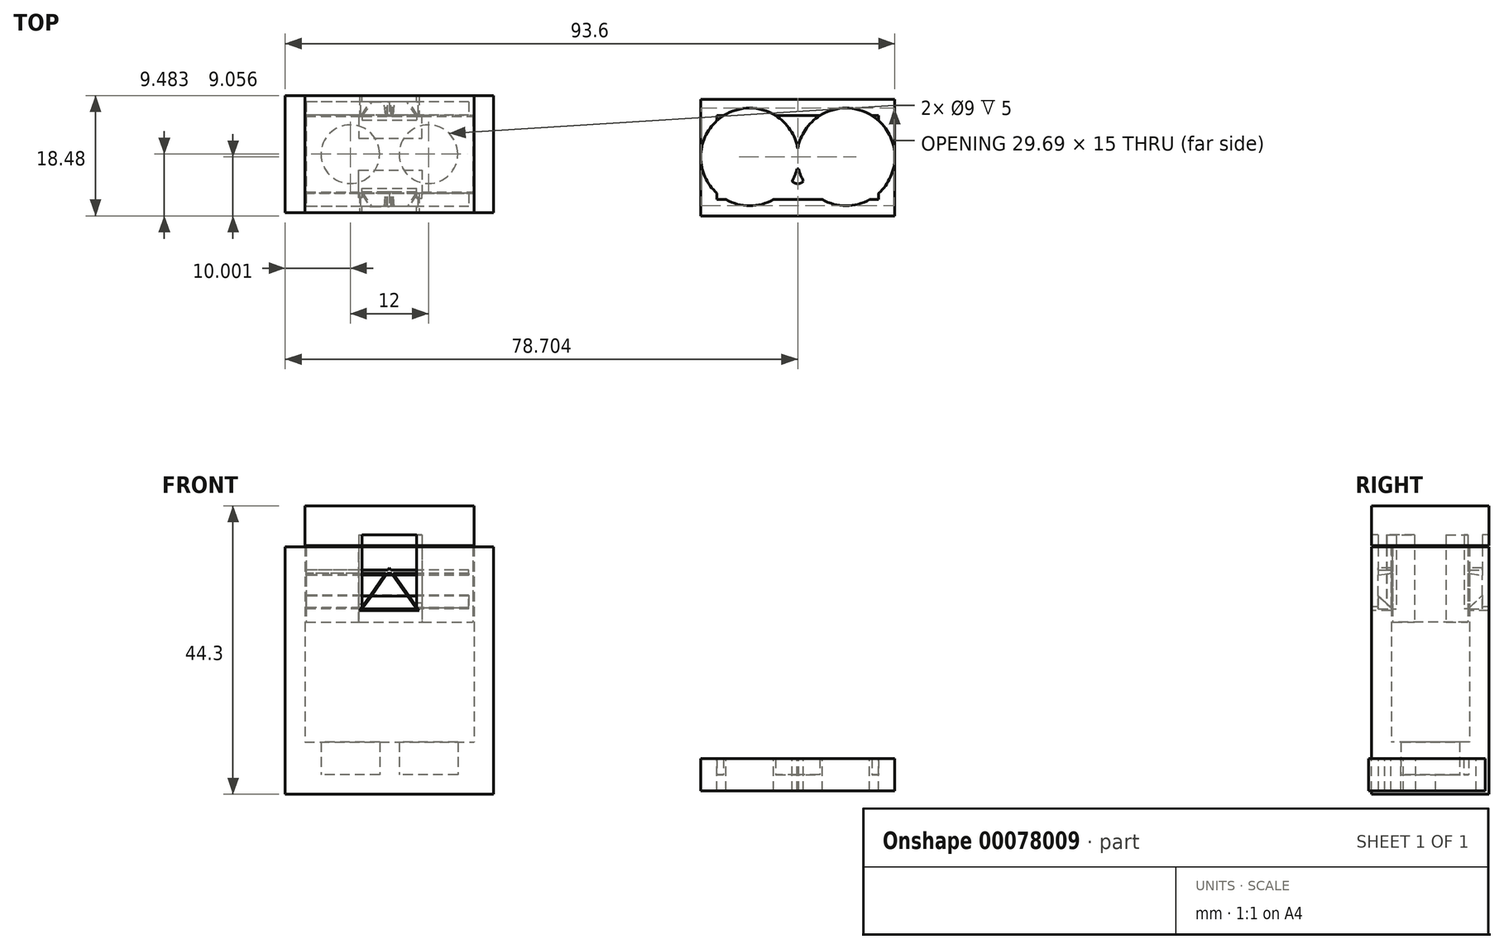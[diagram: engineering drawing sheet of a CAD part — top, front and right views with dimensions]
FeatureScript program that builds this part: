
annotation { "Feature Type Name" : "Feature", "Feature Type Description" : "" }
export const myFeature = defineFeature(function(context is Context, id is Id, definition is map)
    precondition{}
    {
        {
            var Q0;
            Q0=qCreatedBy(makeId("Top.planeOp"),FACE);
            var sketch = newSketch(context, id + "F0", { "sketchPlane" : qUnion([Q0])});
            skCircle(sketch, "E0", {"center": v(-25.55, 16.63) * mm, "radius": 4.5 * mm});
            skCircle(sketch, "E1.1.0.0", {"center": v(-13.55, 16.63) * mm, "radius": 4.5 * mm});
            skLineSegment(sketch, "E1.direction1", {"start": v(-25.55, 16.63) * mm, "end": v(-13.55, 16.63) * mm, "construction": true});
            skLineSegment(sketch, "E2.bottom", {"start": v(-32.55, 22.63) * mm, "end": v(-6.55, 22.63) * mm});
            skLineSegment(sketch, "E2.top", {"start": v(-32.55, 10.63) * mm, "end": v(-6.55, 10.63) * mm});
            skLineSegment(sketch, "E2.left", {"start": v(-32.55, 22.63) * mm, "end": v(-32.55, 10.63) * mm});
            skLineSegment(sketch, "E2.right", {"start": v(-6.55, 22.63) * mm, "end": v(-6.55, 10.63) * mm});
            skLineSegment(sketch, "E3", {"start": v(-25.55, 16.63) * mm, "end": v(-32.55, 16.63) * mm, "construction": true});
            skLineSegment(sketch, "E4", {"start": v(-19.55, 22.63) * mm, "end": v(-19.55, 16.63) * mm, "construction": true});
            skLineSegment(sketch, "E5", {"start": v(-19.55, 16.63) * mm, "end": v(-19.55, 10.63) * mm, "construction": true});
            skLineSegment(sketch, "E6.0", {"start": v(-35.55, 25.63) * mm, "end": v(-3.55, 25.63) * mm});
            skLineSegment(sketch, "E6.1", {"start": v(-35.55, 25.63) * mm, "end": v(-35.55, 7.63) * mm});
            skLineSegment(sketch, "E6.2", {"start": v(-35.55, 7.63) * mm, "end": v(-3.55, 7.63) * mm});
            skLineSegment(sketch, "E6.3", {"start": v(-3.55, 25.63) * mm, "end": v(-3.55, 7.63) * mm});
            skSolve(sketch);
        }
        {
            var Q0;
            Q0=makeQuery(id+"F0.imprint","IMPRINT",FACE,{"disambiguationData":[TD([[makeQuery(id+"F0.imprint","IMPRINT",EDGE,{"derivedFrom":sQuery(id+"F0.wireOp",EDGE,"E1.1.0.0")}),1.0]])]});
            var Q1;
            Q1=makeQuery(id+"F0.imprint","IMPRINT",FACE,{"disambiguationData":[TD([[makeQuery(id+"F0.imprint","IMPRINT",EDGE,{"derivedFrom":sQuery(id+"F0.wireOp",EDGE,"E0")}),-1.0]])]});
            var Q2;
            Q2=makeQuery(id+"F0.imprint","IMPRINT",FACE,{"disambiguationData":[TD([[makeQuery(id+"F0.imprint","IMPRINT",EDGE,{"derivedFrom":sQuery(id+"F0.wireOp",EDGE,"E2.bottom")}),1.0]])]});
            var Q3;
            Q3=makeQuery(id+"F0.imprint","IMPRINT",FACE,{"disambiguationData":[TD([[makeQuery(id+"F0.imprint","IMPRINT",EDGE,{"derivedFrom":sQuery(id+"F0.wireOp",EDGE,"E0")}),1.0]])]});
            extrude(context, id + "F1", {"entities" : qUnion([Q0, Q1, Q2, Q3]), "oppositeDirection" : true, "depth" : 3 * mm});
        }
        {
            var Q0;
            Q0=makeQuery(id+"F0.imprint","IMPRINT",FACE,{"disambiguationData":[TD([[makeQuery(id+"F0.imprint","IMPRINT",EDGE,{"derivedFrom":sQuery(id+"F0.wireOp",EDGE,"E0")}),-1.0]])]});
            extrude(context, id + "F2", {"entities" : qUnion([Q0]), "operationType" : NewBodyOperationType.ADD, "depth" : 5 * mm});
        }
        {
            var Q0;
            Q0=makeQuery(id+"F0.imprint","IMPRINT",FACE,{"disambiguationData":[TD([[makeQuery(id+"F0.imprint","IMPRINT",EDGE,{"derivedFrom":sQuery(id+"F0.wireOp",EDGE,"E2.bottom")}),1.0]])]});
            extrude(context, id + "F3", {"entities" : qUnion([Q0]), "operationType" : NewBodyOperationType.ADD, "depth" : 35 * mm});
        }
        {
            var Q0;
            {var subQ0=sQuery(id+"F0.wireOp",EDGE,"E6.2");Q0=makeQuery(id+"F3.boolean.opBoolean","MERGE",FACE,{"derivedFrom":[makeQuery(id+"F1.opExtrude","SWEPT_FACE",FACE,{"disambiguationData":[OSD([subQ0])]}),makeQuery(id+"F3.opExtrude","SWEPT_FACE",FACE,{"disambiguationData":[OSD([subQ0])]})]});}
            var sketch = newSketch(context, id + "F4", { "sketchPlane" : qUnion([Q0])});
            skLineSegment(sketch, "E7.0", {"start": v(-32.55, 0) * mm, "end": v(-6.55, 0) * mm});
            skLineSegment(sketch, "E8", {"start": v(-32.55, 0) * mm, "end": v(-32.55, 31.77) * mm});
            skLineSegment(sketch, "E9", {"start": v(-6.55, 0) * mm, "end": v(-6.55, 31.77) * mm});
            skLineSegment(sketch, "E10", {"start": v(-6.55, 31.77) * mm, "end": v(-32.55, 31.77) * mm});
            skLineSegment(sketch, "E11", {"start": v(-19.55, 31.77) * mm, "end": v(-19.55, 25.23) * mm, "construction": true});
            skLineSegment(sketch, "E12", {"start": v(-19.55, 25.23) * mm, "end": v(-14.96, 25.23) * mm});
            skLineSegment(sketch, "E13", {"start": v(-14.96, 25.23) * mm, "end": v(-19.55, 31.77) * mm});
            skLineSegment(sketch, "E14.MirrorCS", {"start": v(-19.55, 25.23) * mm, "end": v(-24.13, 25.23) * mm});
            skLineSegment(sketch, "E15.MirrorCS", {"start": v(-24.13, 25.23) * mm, "end": v(-19.55, 31.77) * mm});
            skLineSegment(sketch, "E16", {"start": v(-32.55, 25.46) * mm, "end": v(-6.55, 25.46) * mm});
            skLineSegment(sketch, "E17", {"start": v(-32.55, 31.77) * mm, "end": v(-32.55, 41.3) * mm});
            skLineSegment(sketch, "E18", {"start": v(-32.55, 41.3) * mm, "end": v(-6.55, 41.3) * mm});
            skLineSegment(sketch, "E19", {"start": v(-6.55, 41.3) * mm, "end": v(-6.55, 31.77) * mm});
            skSolve(sketch);
        }
        {
            var Q0;
            Q0=makeQuery(id+"F4.imprint","IMPRINT",FACE,{"disambiguationData":[TD([[makeQuery(id+"F4.imprint","IMPRINT",EDGE,{"derivedFrom":sQuery(id+"F4.wireOp",EDGE,"E12")}),1.0]])]});
            var Q1;
            {var subQ1=sQuery(id+"F4.wireOp",EDGE,"E13");var subQ3=sQuery(id+"F4.wireOp",EDGE,"E16");var subQ4=makeQuery(id+"F4.imprint","INTERSECT",VERTEX,{"derivedFrom":[subQ1,subQ3]});Q1=makeQuery(id+"F4.imprint","IMPRINT",FACE,{"disambiguationData":[TD([[makeQuery(id+"F4.imprint","IMPRINT",EDGE,{"disambiguationData":[TD([[subQ4,1.0]])],"derivedFrom":subQ3}),1.0]])]});}
            var Q2;
            {var subQ0=sQuery(id+"F0.wireOp",EDGE,"E6.0");Q2=makeQuery(id+"F3.boolean.opBoolean","MERGE",FACE,{"derivedFrom":[makeQuery(id+"F1.opExtrude","SWEPT_FACE",FACE,{"disambiguationData":[OSD([subQ0])]}),makeQuery(id+"F3.opExtrude","SWEPT_FACE",FACE,{"disambiguationData":[OSD([subQ0])]})]});}
            var Q3;
            Q3=makeQuery(id+"F1.opExtrude","SWEPT_BODY",BODY,{"disambiguationData":[OSD([sQuery(id+"F0.wireOp",EDGE,"E6.0"),sQuery(id+"F0.wireOp",EDGE,"E6.1"),sQuery(id+"F0.wireOp",EDGE,"E6.2"),sQuery(id+"F0.wireOp",EDGE,"E6.3")])]});
            extrude(context, id + "F5", {"entities" : qUnion([Q0, Q1]), "operationType" : NewBodyOperationType.REMOVE, "endBound" : BoundingType.UP_TO_SURFACE, "oppositeDirection" : true, "endBoundEntityFace" : qUnion([Q2]), "endBoundEntityBody" : qUnion([Q3]), "depth" : 25 * mm});
        }
        {
            var Q0;
            {var subQ0=sQuery(id+"F4.wireOp",EDGE,"E18");Q0=makeQuery(id+"F4.imprint","IMPRINT",FACE,{"disambiguationData":[TD([[makeQuery(id+"F4.imprint","IMPRINT",EDGE,{"derivedFrom":subQ0}),-1.0]])]});}
            var Q1;
            {var subQ0=sQuery(id+"F4.wireOp",EDGE,"E17");var subQ3=makeQuery(id+"F3.opExtrude","CAP_EDGE",EDGE,{"disambiguationData":[OSD([sQuery(id+"F0.wireOp",EDGE,"E6.2")])],"isStart":false});var subQ4=makeQuery(id+"F4.imprint","INTERSECT",VERTEX,{"derivedFrom":[subQ3,subQ0]});Q1=makeQuery(id+"F4.imprint","IMPRINT",FACE,{"disambiguationData":[TD([[makeQuery(id+"F4.imprint","IMPRINT",EDGE,{"disambiguationData":[TD([[subQ4,-1.0]])],"derivedFrom":subQ3}),-1.0]])]});}
            var Q2;
            {var subQ1=sQuery(id+"F4.wireOp",EDGE,"E8");var subQ3=sQuery(id+"F4.wireOp",EDGE,"E16");var subQ4=makeQuery(id+"F4.imprint","INTERSECT",VERTEX,{"derivedFrom":[subQ1,subQ3]});Q2=makeQuery(id+"F4.imprint","IMPRINT",FACE,{"disambiguationData":[TD([[makeQuery(id+"F4.imprint","IMPRINT",EDGE,{"disambiguationData":[TD([[subQ4,-1.0]])],"derivedFrom":subQ3}),1.0]])]});}
            var Q3;
            {var subQ1=sQuery(id+"F4.wireOp",EDGE,"E13");var subQ3=sQuery(id+"F4.wireOp",EDGE,"E16");var subQ4=makeQuery(id+"F4.imprint","INTERSECT",VERTEX,{"derivedFrom":[subQ1,subQ3]});Q3=makeQuery(id+"F4.imprint","IMPRINT",FACE,{"disambiguationData":[TD([[makeQuery(id+"F4.imprint","IMPRINT",EDGE,{"disambiguationData":[TD([[subQ4,1.0]])],"derivedFrom":subQ3}),1.0]])]});}
            var Q4;
            {var subQ1=sQuery(id+"F4.wireOp",EDGE,"E9");var subQ3=sQuery(id+"F4.wireOp",EDGE,"E16");var subQ4=makeQuery(id+"F4.imprint","INTERSECT",VERTEX,{"derivedFrom":[subQ1,subQ3]});Q4=makeQuery(id+"F4.imprint","IMPRINT",FACE,{"disambiguationData":[TD([[makeQuery(id+"F4.imprint","IMPRINT",EDGE,{"disambiguationData":[TD([[subQ4,1.0]])],"derivedFrom":subQ3}),1.0]])]});}
            var Q5;
            {var subQ0=sQuery(id+"F0.wireOp",EDGE,"E6.0");Q5=makeQuery(id+"F3.boolean.opBoolean","MERGE",FACE,{"derivedFrom":[makeQuery(id+"F1.opExtrude","SWEPT_FACE",FACE,{"disambiguationData":[OSD([subQ0])]}),makeQuery(id+"F3.opExtrude","SWEPT_FACE",FACE,{"disambiguationData":[OSD([subQ0])]})]});}
            extrude(context, id + "F6", {"entities" : qUnion([Q0, Q1, Q2, Q3, Q4]), "endBound" : BoundingType.UP_TO_SURFACE, "oppositeDirection" : true, "endBoundEntityFace" : qUnion([Q5]), "depth" : 25 * mm});
        }
        {
            var Q0;
            Q0=makeQuery(id+"F1.opExtrude","SWEPT_BODY",BODY,{"disambiguationData":[OSD([sQuery(id+"F0.wireOp",EDGE,"E6.0"),sQuery(id+"F0.wireOp",EDGE,"E6.1"),sQuery(id+"F0.wireOp",EDGE,"E6.2"),sQuery(id+"F0.wireOp",EDGE,"E6.3")])]});
            var Q1;
            Q1=makeQuery(id+"F6.opExtrude","SWEPT_BODY",BODY,{"disambiguationData":[OSD([sQuery(id+"F4.wireOp",EDGE,"E8"),sQuery(id+"F4.wireOp",EDGE,"E9"),sQuery(id+"F4.wireOp",EDGE,"E16"),sQuery(id+"F4.wireOp",EDGE,"E17"),sQuery(id+"F4.wireOp",EDGE,"E18"),sQuery(id+"F4.wireOp",EDGE,"E19")])]});
            booleanBodies(context, id + "F7", {"operationType" : BooleanOperationType.SUBTRACTION, "tools" : qUnion([Q0]), "targets" : qUnion([Q1]), "offset" : true, "offsetAll" : true, "offsetDistance" : 0.2 * mm, "keepTools" : true});
        }
        {
            var Q0;
            Q0=makeQuery(id+"F6.opExtrude","SWEPT_FACE",FACE,{"disambiguationData":[OSD([sQuery(id+"F4.wireOp",EDGE,"E16")])]});
            var sketch = newSketch(context, id + "F8", { "sketchPlane" : qUnion([Q0])});
            skLineSegment(sketch, "E20", {"start": v(-23.73, -10.83) * mm, "end": v(-23.73, -11.42) * mm});
            skLineSegment(sketch, "E21", {"start": v(-23.73, -11.42) * mm, "end": v(-15.37, -11.42) * mm});
            skLineSegment(sketch, "E22", {"start": v(-15.37, -10.83) * mm, "end": v(-15.37, -11.42) * mm});
            skLineSegment(sketch, "E23", {"start": v(-24.25, -10.83) * mm, "end": v(-24.25, -14.2) * mm});
            skLineSegment(sketch, "E24", {"start": v(-24.25, -14.2) * mm, "end": v(-14.57, -14.2) * mm});
            skLineSegment(sketch, "E25", {"start": v(-14.57, -14.2) * mm, "end": v(-14.57, -10.83) * mm});
            skLineSegment(sketch, "E26", {"start": v(-23.73, -8.63) * mm, "end": v(-15.37, -8.63) * mm});
            skLineSegment(sketch, "E27", {"start": v(-32.35, -16.63) * mm, "end": v(-6.75, -16.63) * mm, "construction": true});
            skLineSegment(sketch, "E28.MirrorCS", {"start": v(-24.25, -19.07) * mm, "end": v(-14.57, -19.07) * mm});
            skLineSegment(sketch, "E29.MirrorCS", {"start": v(-14.57, -19.07) * mm, "end": v(-14.57, -22.43) * mm});
            skLineSegment(sketch, "E30.MirrorCS", {"start": v(-23.73, -21.85) * mm, "end": v(-15.37, -21.85) * mm});
            skLineSegment(sketch, "E31.MirrorCS", {"start": v(-24.25, -22.43) * mm, "end": v(-24.25, -19.07) * mm});
            skLineSegment(sketch, "E32.MirrorCS", {"start": v(-23.73, -22.43) * mm, "end": v(-23.73, -21.85) * mm});
            skLineSegment(sketch, "E33.MirrorCS", {"start": v(-15.37, -22.43) * mm, "end": v(-15.37, -21.85) * mm});
            skLineSegment(sketch, "E34.MirrorCS", {"start": v(-23.73, -24.64) * mm, "end": v(-15.37, -24.64) * mm});
            skLineSegment(sketch, "E35", {"start": v(-24.25, -10.83) * mm, "end": v(-24.25, -9.96) * mm});
            skLineSegment(sketch, "E36", {"start": v(-24.25, -9.96) * mm, "end": v(-23.73, -9.96) * mm});
            skLineSegment(sketch, "E37", {"start": v(-14.57, -10.83) * mm, "end": v(-14.57, -9.88) * mm});
            skLineSegment(sketch, "E38", {"start": v(-14.57, -9.88) * mm, "end": v(-15.37, -9.88) * mm});
            skSolve(sketch);
        }
        {
            var Q0;
            {var subQ2=sQuery(id+"F8.wireOp",EDGE,"E20");Q0=makeQuery(id+"F8.imprint","IMPRINT",FACE,{"disambiguationData":[TD([[makeQuery(id+"F8.imprint","IMPRINT",EDGE,{"derivedFrom":subQ2}),-1.0]])]});}
            var Q1;
            {var subQ0=sQuery(id+"F8.wireOp",EDGE,"E26");Q1=makeQuery(id+"F8.imprint","IMPRINT",FACE,{"disambiguationData":[TD([[makeQuery(id+"F8.imprint","IMPRINT",EDGE,{"derivedFrom":subQ0}),1.0]])]});}
            var Q2;
            {var subQ0=sQuery(id+"F8.wireOp",EDGE,"E34.MirrorCS");Q2=makeQuery(id+"F8.imprint","IMPRINT",FACE,{"disambiguationData":[TD([[makeQuery(id+"F8.imprint","IMPRINT",EDGE,{"derivedFrom":subQ0}),-1.0]])]});}
            var Q3;
            {var subQ0=sQuery(id+"F8.wireOp",EDGE,"E37");Q3=makeQuery(id+"F8.imprint","IMPRINT",FACE,{"disambiguationData":[TD([[makeQuery(id+"F8.imprint","IMPRINT",EDGE,{"derivedFrom":subQ0}),1.0]])]});}
            var Q4;
            {var subQ0=sQuery(id+"F8.wireOp",EDGE,"E35");Q4=makeQuery(id+"F8.imprint","IMPRINT",FACE,{"disambiguationData":[TD([[makeQuery(id+"F8.imprint","IMPRINT",EDGE,{"derivedFrom":subQ0}),-1.0]])]});}
            var Q5;
            Q5=makeQuery(id+"F8.imprint","IMPRINT",FACE,{"disambiguationData":[TD([[makeQuery(id+"F8.imprint","IMPRINT",EDGE,{"derivedFrom":sQuery(id+"F8.wireOp",EDGE,"E28.MirrorCS")}),-1.0]])]});
            extrude(context, id + "F9", {"entities" : qUnion([Q0, Q1, Q2, Q3, Q4, Q5]), "operationType" : NewBodyOperationType.REMOVE, "oppositeDirection" : true, "depth" : 11.34 * mm});
        }
        {
            var Q0;
            Q0=makeQuery(id+"F9.boolean.opBoolean","SPLIT",FACE,{"disambiguationData":[TD([makeQuery(id+"F7.tempBoolean.opBoolean","COPY",FACE,{"derivedFrom":makeQuery(id+"F7.offsetTempBody.opPattern","COPY",FACE,{"derivedFrom":makeQuery(id+"F3.opExtrude","SWEPT_FACE",FACE,{"disambiguationData":[OSD([sQuery(id+"F0.wireOp",EDGE,"E2.left")])]}),"instanceName":"1"})})])],"derivedFrom":makeQuery(id+"F6.opExtrude","SWEPT_FACE",FACE,{"disambiguationData":[OSD([sQuery(id+"F4.wireOp",EDGE,"E16")])]})});
            extrude(context, id + "F10", {"entities" : qUnion([Q0]), "operationType" : NewBodyOperationType.ADD, "depth" : 2 * mm});
        }
        {
            var Q0;
            {var subQ0=sQuery(id+"F0.wireOp",EDGE,"E2.left");Q0=makeQuery(id+"F10.boolean.opBoolean","MERGE",FACE,{"derivedFrom":[makeQuery(id+"F7.tempBoolean.opBoolean","COPY",FACE,{"derivedFrom":makeQuery(id+"F7.offsetTempBody.opPattern","COPY",FACE,{"derivedFrom":makeQuery(id+"F3.opExtrude","SWEPT_FACE",FACE,{"disambiguationData":[OSD([subQ0])]}),"instanceName":"1"})}),makeQuery(id+"F10.opExtrude","SWEPT_FACE",FACE,{"disambiguationData":[OSD([subQ0,sQuery(id+"F4.wireOp",EDGE,"E16")])]})]});}
            var sketch = newSketch(context, id + "F11", { "sketchPlane" : qUnion([Q0])});
            skLineSegment(sketch, "E39.0", {"start": v(-24.64, 31.43) * mm, "end": v(-22.43, 31.43) * mm});
            skLineSegment(sketch, "E40.0", {"start": v(-24.64, 25.46) * mm, "end": v(-24.64, 31.43) * mm});
            skLineSegment(sketch, "E41.0", {"start": v(-24.64, 25.46) * mm, "end": v(-22.43, 25.46) * mm});
            skLineSegment(sketch, "E42.0", {"start": v(-10.83, 25.46) * mm, "end": v(-8.63, 25.46) * mm});
            skLineSegment(sketch, "E43.0", {"start": v(-8.63, 25.46) * mm, "end": v(-8.63, 31.43) * mm});
            skLineSegment(sketch, "E44.0", {"start": v(-10.83, 31.43) * mm, "end": v(-8.63, 31.43) * mm});
            skLineSegment(sketch, "E45", {"start": v(-24.64, 27.58) * mm, "end": v(-22.43, 25.46) * mm});
            skLineSegment(sketch, "E46", {"start": v(-8.63, 27.46) * mm, "end": v(-10.83, 25.46) * mm});
            skLineSegment(sketch, "E47", {"start": v(-24.64, 30.63) * mm, "end": v(-22.43, 30.92) * mm});
            skLineSegment(sketch, "E48", {"start": v(-10.83, 30.92) * mm, "end": v(-8.63, 30.7) * mm});
            skSolve(sketch);
        }
        {
            var Q0;
            {var subQ0=sQuery(id+"F11.wireOp",EDGE,"E39.0");Q0=makeQuery(id+"F11.imprint","IMPRINT",FACE,{"disambiguationData":[TD([[makeQuery(id+"F11.imprint","IMPRINT",EDGE,{"derivedFrom":subQ0}),-1.0]])]});}
            var Q1;
            {var subQ0=sQuery(id+"F11.wireOp",EDGE,"E41.0");Q1=makeQuery(id+"F11.imprint","IMPRINT",FACE,{"disambiguationData":[TD([[makeQuery(id+"F11.imprint","IMPRINT",EDGE,{"derivedFrom":subQ0}),1.0]])]});}
            var Q2;
            {var subQ0=sQuery(id+"F11.wireOp",EDGE,"E42.0");Q2=makeQuery(id+"F11.imprint","IMPRINT",FACE,{"disambiguationData":[TD([[makeQuery(id+"F11.imprint","IMPRINT",EDGE,{"derivedFrom":subQ0}),1.0]])]});}
            var Q3;
            {var subQ0=sQuery(id+"F11.wireOp",EDGE,"E44.0");Q3=makeQuery(id+"F11.imprint","IMPRINT",FACE,{"disambiguationData":[TD([[makeQuery(id+"F11.imprint","IMPRINT",EDGE,{"derivedFrom":subQ0}),-1.0]])]});}
            extrude(context, id + "F12", {"entities" : qUnion([Q0, Q1, Q2, Q3]), "operationType" : NewBodyOperationType.REMOVE, "oppositeDirection" : true, "depth" : 25 * mm});
        }
        {
            var Q0;
            Q0=qCreatedBy(makeId("Top.planeOp"),FACE);
            var sketch = newSketch(context, id + "F13", { "sketchPlane" : qUnion([Q0])});
            skLineSegment(sketch, "E49.bottom", {"start": v(30.75, 22.55) * mm, "end": v(55.55, 22.55) * mm});
            skLineSegment(sketch, "E49.top", {"start": v(30.75, 9.65) * mm, "end": v(55.55, 9.65) * mm});
            skLineSegment(sketch, "E49.left", {"start": v(30.75, 22.55) * mm, "end": v(30.75, 9.65) * mm});
            skLineSegment(sketch, "E49.right", {"start": v(55.55, 22.55) * mm, "end": v(55.55, 9.65) * mm});
            skLineSegment(sketch, "E50", {"start": v(43.15, 22.55) * mm, "end": v(43.15, 9.65) * mm, "construction": true});
            skCircle(sketch, "E51", {"center": v(43.15, 13.25) * mm, "radius": 1.15 * mm});
            skLineSegment(sketch, "E52.0", {"start": v(28.25, 25.05) * mm, "end": v(58.05, 25.05) * mm});
            skLineSegment(sketch, "E52.1", {"start": v(28.25, 25.05) * mm, "end": v(28.25, 7.15) * mm});
            skLineSegment(sketch, "E52.2", {"start": v(28.25, 7.15) * mm, "end": v(58.05, 7.15) * mm});
            skLineSegment(sketch, "E52.3", {"start": v(58.05, 25.05) * mm, "end": v(58.05, 7.15) * mm});
            skLineSegment(sketch, "E53", {"start": v(30.75, 16.1) * mm, "end": v(55.55, 16.1) * mm, "construction": true});
            skCircle(sketch, "E54", {"center": v(35.76, 16.2) * mm, "radius": 7.5 * mm});
            skCircle(sketch, "E55.MirrorC", {"center": v(50.55, 16.2) * mm, "radius": 7.5 * mm});
            skSolve(sketch);
        }
        {
            var Q0;
            Q0=makeQuery(id+"F13.imprint","IMPRINT",FACE,{"disambiguationData":[TD([[makeQuery(id+"F13.imprint","IMPRINT",EDGE,{"derivedFrom":sQuery(id+"F13.wireOp",EDGE,"E49.bottom")}),1.0]])]});
            var Q1;
            Q1=makeQuery(id+"F13.imprint","IMPRINT",FACE,{"disambiguationData":[TD([[makeQuery(id+"F13.imprint","IMPRINT",EDGE,{"derivedFrom":sQuery(id+"F13.wireOp",EDGE,"E49.bottom")}),-1.0]])]});
            var Q2;
            Q2=makeQuery(id+"F13.imprint","IMPRINT",FACE,{"disambiguationData":[TD([[makeQuery(id+"F13.imprint","IMPRINT",EDGE,{"derivedFrom":sQuery(id+"F13.wireOp",EDGE,"E51")}),1.0]])]});
            extrude(context, id + "F14", {"entities" : qUnion([Q0, Q1, Q2]), "oppositeDirection" : true, "depth" : 2.5 * mm});
        }
        {
            var Q0;
            Q0=makeQuery(id+"F13.imprint","IMPRINT",FACE,{"disambiguationData":[TD([[makeQuery(id+"F13.imprint","IMPRINT",EDGE,{"derivedFrom":sQuery(id+"F13.wireOp",EDGE,"E49.bottom")}),1.0]])]});
            var sketch = newSketch(context, id + "F15", { "sketchPlane" : qUnion([Q0])});
            skSolve(sketch);
        }
        {
            var Q0;
            Q0 = qSketchRegion(id + "F15", true);
            var Q1;
            Q1=makeQuery(id+"F13.imprint","IMPRINT",FACE,{"disambiguationData":[TD([[makeQuery(id+"F13.imprint","IMPRINT",EDGE,{"derivedFrom":sQuery(id+"F13.wireOp",EDGE,"E49.bottom")}),1.0]])]});
            var Q2;
            Q2=makeQuery(id+"F13.imprint","IMPRINT",FACE,{"disambiguationData":[TD([[makeQuery(id+"F13.imprint","IMPRINT",EDGE,{"derivedFrom":sQuery(id+"F13.wireOp",EDGE,"E51")}),1.0]])]});
            extrude(context, id + "F16", {"entities" : qUnion([Q0, Q1, Q2]), "operationType" : NewBodyOperationType.ADD, "depth" : 2.5 * mm});
        }
    });
